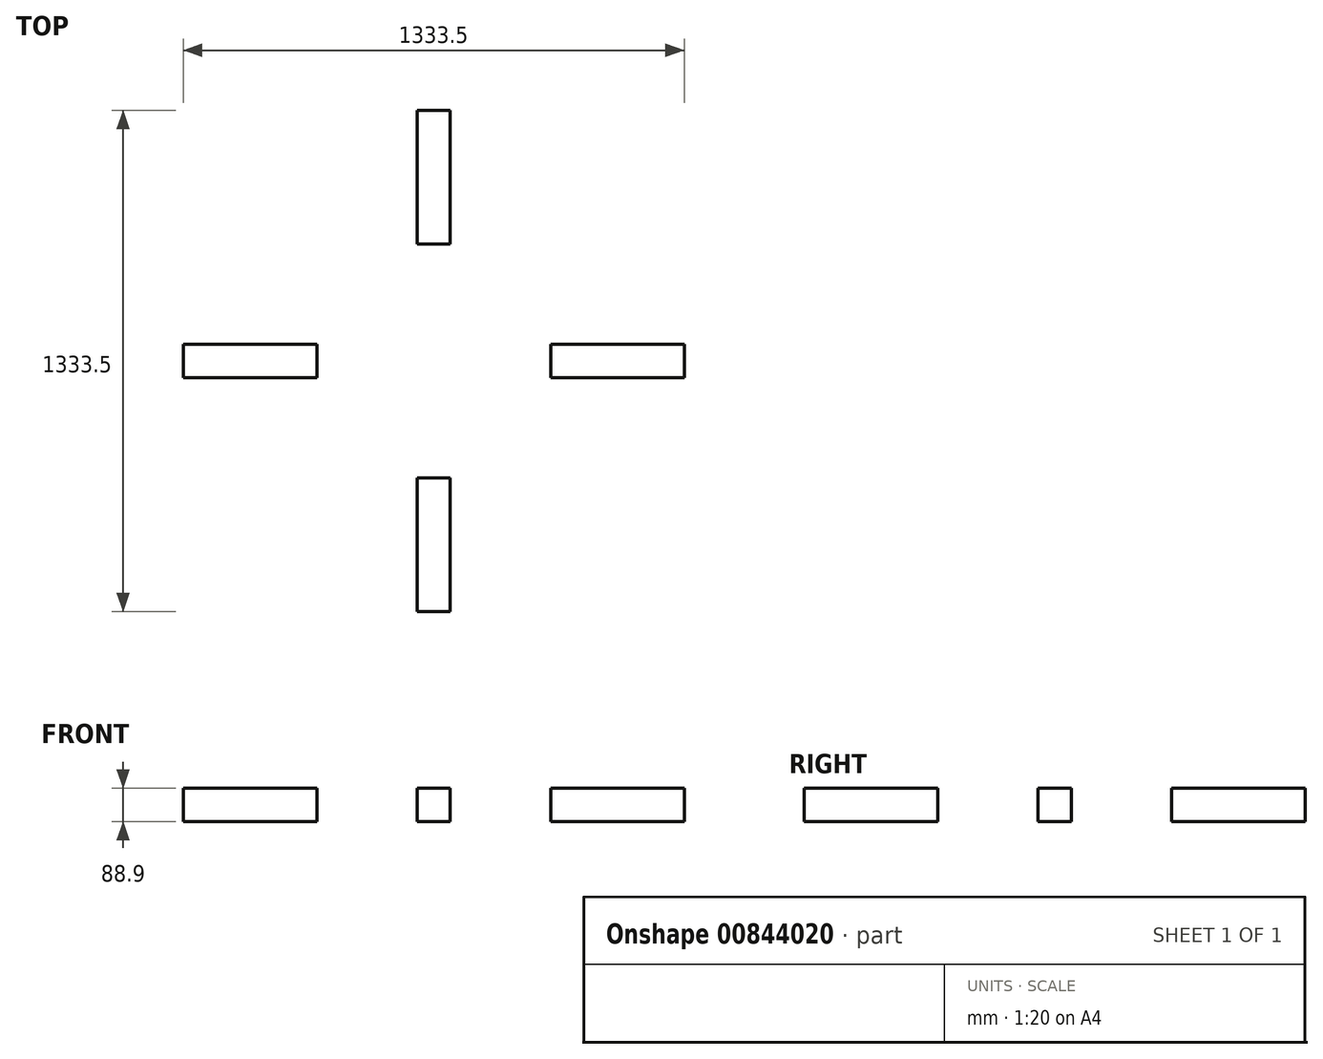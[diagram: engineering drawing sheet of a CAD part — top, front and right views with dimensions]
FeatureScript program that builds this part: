
annotation { "Feature Type Name" : "Feature", "Feature Type Description" : "" }
export const myFeature = defineFeature(function(context is Context, id is Id, definition is map)
    precondition{}
    {
        {
            var Q0;
            Q0=qCreatedBy(makeId("Top.planeOp"),FACE);
            var sketch = newSketch(context, id + "F0", { "sketchPlane" : qUnion([Q0])});
            skLineSegment(sketch, "E0.bottom", {"start": v(-666.75, 44.45) * mm, "end": v(-311.15, 44.45) * mm});
            skLineSegment(sketch, "E0.top", {"start": v(-666.75, -44.45) * mm, "end": v(-311.15, -44.45) * mm});
            skLineSegment(sketch, "E0.left", {"start": v(-666.75, 44.45) * mm, "end": v(-666.75, -44.45) * mm});
            skLineSegment(sketch, "E0.right", {"start": v(-311.15, 44.45) * mm, "end": v(-311.15, -44.45) * mm});
            skLineSegment(sketch, "E1.bottom", {"start": v(311.15, 44.45) * mm, "end": v(666.75, 44.45) * mm});
            skLineSegment(sketch, "E1.top", {"start": v(311.15, -44.45) * mm, "end": v(666.75, -44.45) * mm});
            skLineSegment(sketch, "E1.left", {"start": v(311.15, 44.45) * mm, "end": v(311.15, -44.45) * mm});
            skLineSegment(sketch, "E1.right", {"start": v(666.75, 44.45) * mm, "end": v(666.75, -44.45) * mm});
            skPoint(sketch, "E2", {"position": v(666.75, 0) * mm});
            skLineSegment(sketch, "E3.bottom", {"start": v(-44.45, 666.75) * mm, "end": v(44.45, 666.75) * mm});
            skLineSegment(sketch, "E3.top", {"start": v(-44.45, 311.15) * mm, "end": v(44.45, 311.15) * mm});
            skLineSegment(sketch, "E3.left", {"start": v(-44.45, 666.75) * mm, "end": v(-44.45, 311.15) * mm});
            skLineSegment(sketch, "E3.right", {"start": v(44.45, 666.75) * mm, "end": v(44.45, 311.15) * mm});
            skPoint(sketch, "E4", {"position": v(0, 311.15) * mm});
            skLineSegment(sketch, "E5.bottom", {"start": v(-44.45, -311.15) * mm, "end": v(44.45, -311.15) * mm});
            skLineSegment(sketch, "E5.top", {"start": v(-44.45, -666.75) * mm, "end": v(44.45, -666.75) * mm});
            skLineSegment(sketch, "E5.left", {"start": v(-44.45, -311.15) * mm, "end": v(-44.45, -666.75) * mm});
            skLineSegment(sketch, "E5.right", {"start": v(44.45, -311.15) * mm, "end": v(44.45, -666.75) * mm});
            skLineSegment(sketch, "E6", {"start": v(-666.75, -44.45) * mm, "end": v(-666.75, -209.55) * mm});
            skLineSegment(sketch, "E7", {"start": v(-666.75, -209.55) * mm, "end": v(-311.15, -209.55) * mm});
            skLineSegment(sketch, "E8", {"start": v(-311.15, -44.45) * mm, "end": v(-311.15, -209.55) * mm});
            skLineSegment(sketch, "E9", {"start": v(311.15, -44.45) * mm, "end": v(311.15, -209.55) * mm});
            skLineSegment(sketch, "E10", {"start": v(311.15, -209.55) * mm, "end": v(666.75, -209.55) * mm});
            skLineSegment(sketch, "E11", {"start": v(666.75, -209.55) * mm, "end": v(666.75, -44.45) * mm});
            skLineSegment(sketch, "E12.bottom", {"start": v(-152.4, -774.7) * mm, "end": v(152.4, -774.7) * mm});
            skLineSegment(sketch, "E12.top", {"start": v(-152.4, -1079.5) * mm, "end": v(152.4, -1079.5) * mm});
            skLineSegment(sketch, "E12.left", {"start": v(-152.4, -774.7) * mm, "end": v(-152.4, -1079.5) * mm});
            skLineSegment(sketch, "E12.right", {"start": v(152.4, -774.7) * mm, "end": v(152.4, -1079.5) * mm});
            skPoint(sketch, "E13", {"position": v(0, -774.7) * mm});
            skSolve(sketch);
        }
        {
            var Q0;
            Q0=makeQuery(id+"F0.imprint","IMPRINT",FACE,{"disambiguationData":[TD([[makeQuery(id+"F0.imprint","IMPRINT",EDGE,{"derivedFrom":sQuery(id+"F0.wireOp",EDGE,"E0.bottom")}),-1.0]])]});
            var Q1;
            Q1=makeQuery(id+"F0.imprint","IMPRINT",FACE,{"disambiguationData":[TD([[makeQuery(id+"F0.imprint","IMPRINT",EDGE,{"derivedFrom":sQuery(id+"F0.wireOp",EDGE,"E3.bottom")}),-1.0]])]});
            var Q2;
            Q2=makeQuery(id+"F0.imprint","IMPRINT",FACE,{"disambiguationData":[TD([[makeQuery(id+"F0.imprint","IMPRINT",EDGE,{"derivedFrom":sQuery(id+"F0.wireOp",EDGE,"E1.bottom")}),-1.0]])]});
            var Q3;
            Q3=makeQuery(id+"F0.imprint","IMPRINT",FACE,{"disambiguationData":[TD([[makeQuery(id+"F0.imprint","IMPRINT",EDGE,{"derivedFrom":sQuery(id+"F0.wireOp",EDGE,"E5.bottom")}),-1.0]])]});
            extrude(context, id + "F1", {"entities" : qUnion([Q0, Q1, Q2, Q3]), "depth" : 88.9 * mm, "offsetDistance" : 25.4 * mm});
        }
    });
